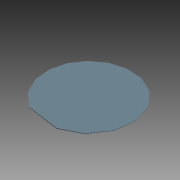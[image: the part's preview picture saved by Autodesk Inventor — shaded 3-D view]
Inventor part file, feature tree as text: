
AUTODESK INVENTOR PART (.ipt)
format: ipt  version: 2011 SP1 (Build 150282100, 282)  size: 109,568 bytes
history: native  units: mm
features: extrude x2, sketch x2, chamfer x1
ambient origin geometry x8: Origin, YZ Plane, XZ Plane, XY Plane, X Axis, Y Axis, Z Axis, Center Point
bodies: Solid1 (feature_tree)
feature tree (5):
  extrude  "Extrusion1"  Depth=100.0mm
  extrude  "Extrusion2"  Depth=0.05mm
  chamfer  "Chamfer2"  Distance=0.25mm
  sketch  "Sketch1"  dims[d1=32.5mm d2=100.0mm]
  sketch  "Sketch2"  dims[d3=0.525mm d4=0.0mm d5=0.05mm d6=0.25mm d7=0.25mm d8=0.025mm d9=0.0mm d13=0.0249mm d14=0.01mm d15=6.161012mm]
